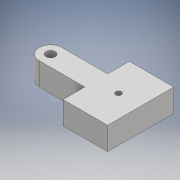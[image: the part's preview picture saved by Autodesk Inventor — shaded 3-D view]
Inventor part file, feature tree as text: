
AUTODESK INVENTOR PART (.ipt)
format: ipt  version: 2017 (Build 210142000, 142)  size: 134,144 bytes
history: native  units: mm
features: extrude x3, sketch x3, projected_geometry x1
ambient origin geometry x8: Origin, YZ Plane, XZ Plane, XY Plane, X Axis, Y Axis, Z Axis, Center Point
bodies: Solid1 (feature_tree)
feature tree (7):
  extrude  "Extrusion1"  Depth=19.05mm
  extrude  "Extrusion2"  Depth=10.0mm
  extrude  "Extrusion3"  Depth=10.0mm
  sketch  "Sketch1"  dims[d0=38.1mm d1=19.05mm]
  sketch  "Sketch2"  dims[d2=10.0mm d3=10.0mm]
  projected_geometry  "Projected Loop1"
  sketch  "Sketch3"  dims[d4=8.0mm d5=10.0mm d6=40.0mm d7=15.0mm d8=0.0mm d9=5.0mm d10=0.0mm d11=5.0mm d12=10.0mm d13=0.0mm]
